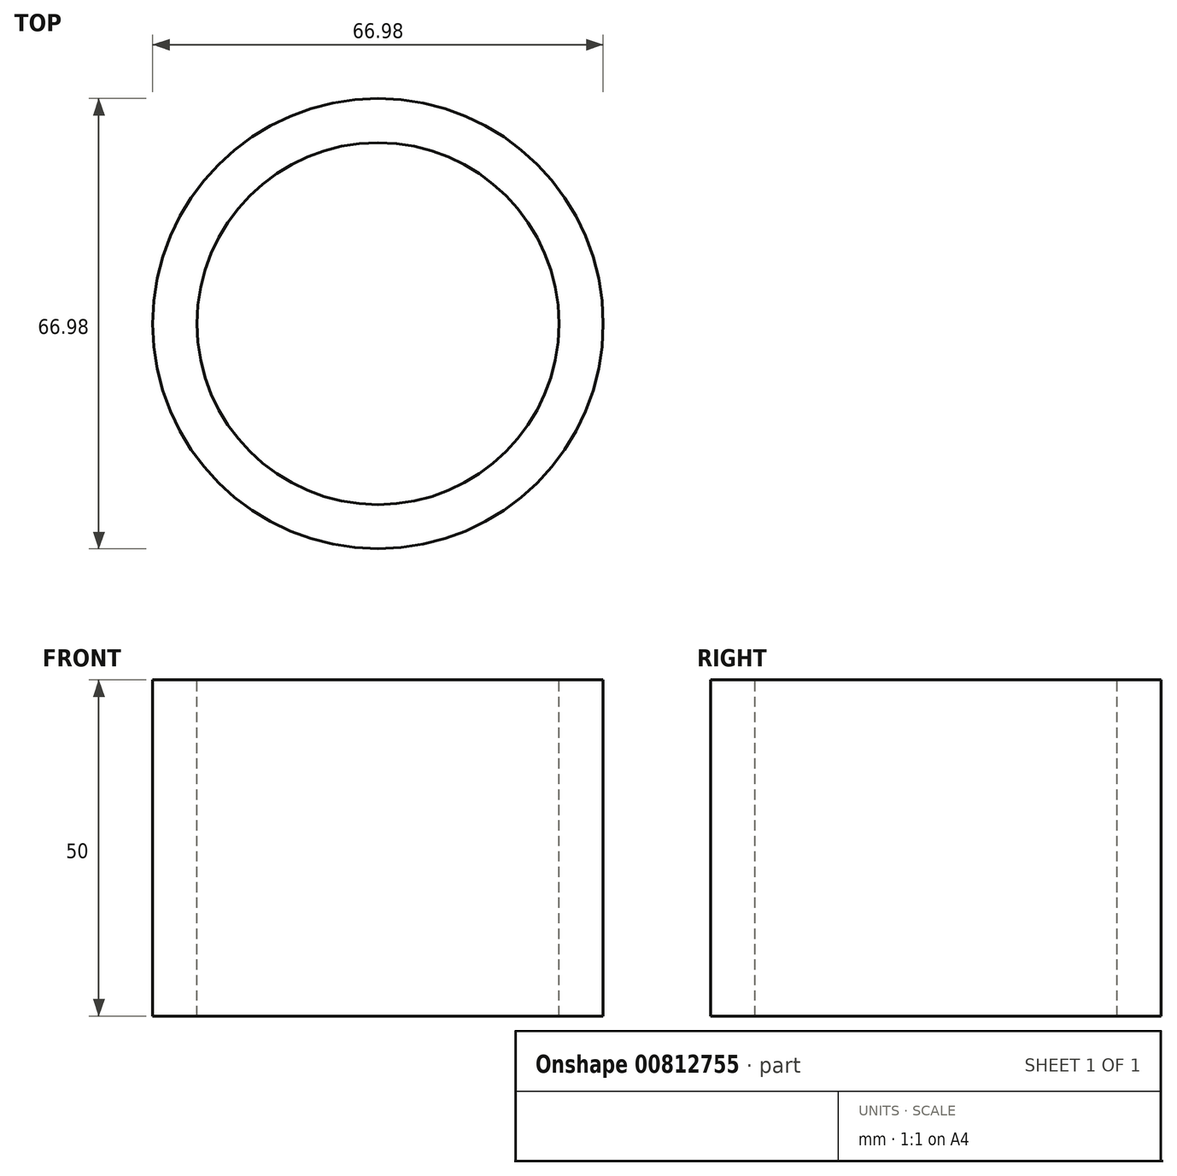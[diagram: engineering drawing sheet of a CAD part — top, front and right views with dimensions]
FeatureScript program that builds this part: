
annotation { "Feature Type Name" : "Feature", "Feature Type Description" : "" }
export const myFeature = defineFeature(function(context is Context, id is Id, definition is map)
    precondition{}
    {
        {
            var Q0;
            Q0=qCreatedBy(makeId("Top.planeOp"),FACE);
            var sketch = newSketch(context, id + "F0", { "sketchPlane" : qUnion([Q0])});
            skCircle(sketch, "E0", {"center": v(0, 0) * mm, "radius": 33.5 * mm});
            skCircle(sketch, "E1", {"center": v(0, 0) * mm, "radius": 26.92 * mm});
            skSolve(sketch);
        }
        {
            var Q0;
            Q0=sQuery(id+"F0.wireOp",EDGE,"E0");
            var Q1;
            Q1=sQuery(id+"F0.wireOp",EDGE,"E1");
            extrude(context, id + "F1", {"bodyType" : ToolBodyType.SURFACE, "surfaceEntities" : qUnion([Q0, Q1]), "depth" : 50 * mm, "offsetDistance" : 25 * mm});
        }
    });
